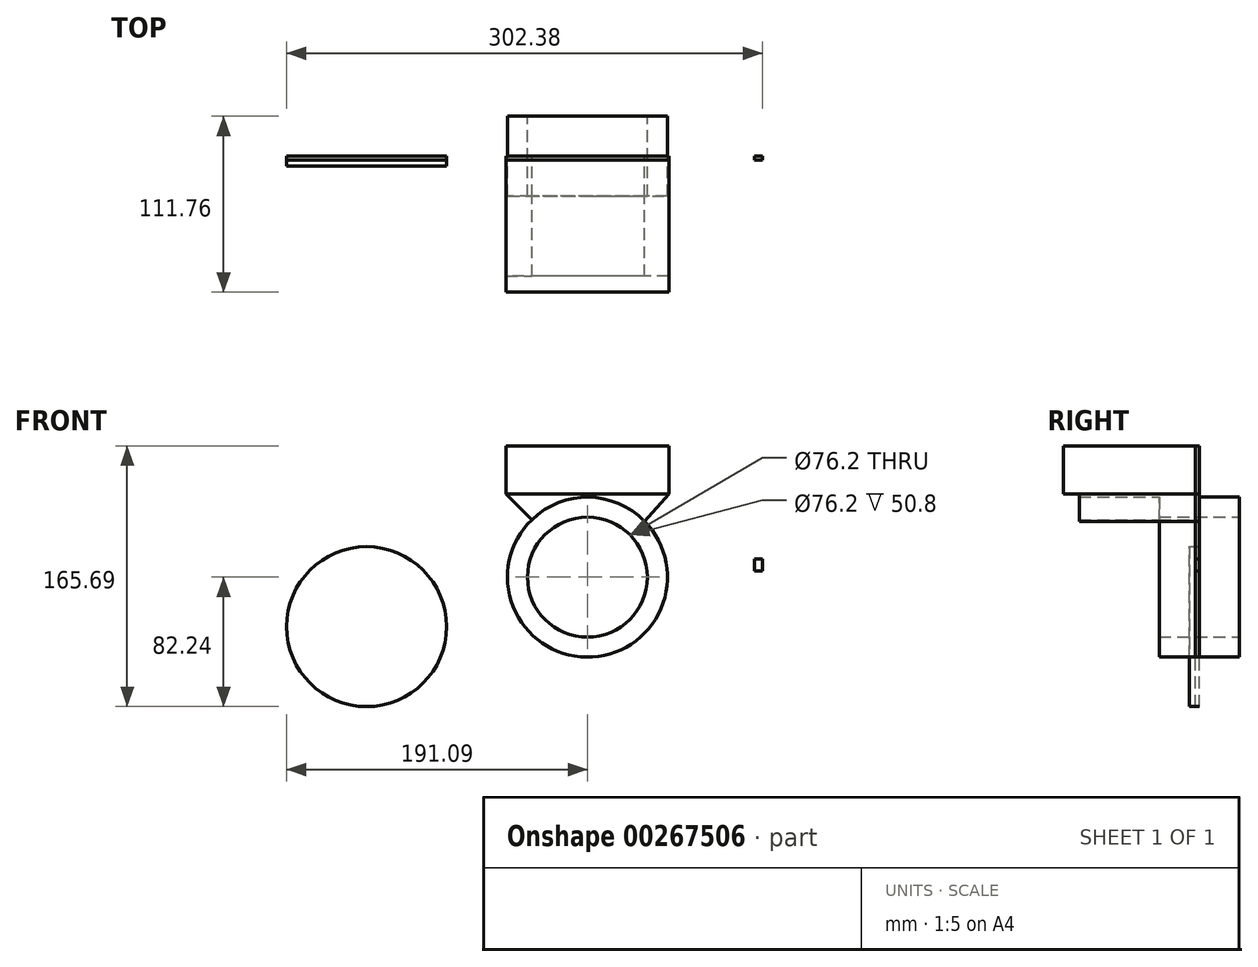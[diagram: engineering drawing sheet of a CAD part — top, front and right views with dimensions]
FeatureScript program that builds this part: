
annotation { "Feature Type Name" : "Feature", "Feature Type Description" : "" }
export const myFeature = defineFeature(function(context is Context, id is Id, definition is map)
    precondition{}
    {
        {
            var Q0;
            Q0=qCreatedBy(makeId("Front.planeOp"),FACE);
            var sketch = newSketch(context, id + "F0", { "sketchPlane" : qUnion([Q0])});
            skCircle(sketch, "E0", {"center": v(0, 0) * mm, "radius": 50.8 * mm});
            skCircle(sketch, "E1", {"center": v(0, 0) * mm, "radius": 38.1 * mm});
            skLineSegment(sketch, "E2.bottom", {"start": v(51.8, 83.45) * mm, "end": v(-51.8, 83.45) * mm});
            skLineSegment(sketch, "E2.top", {"start": v(51.8, 52.8) * mm, "end": v(-51.8, 52.8) * mm});
            skLineSegment(sketch, "E2.left", {"start": v(51.8, 83.45) * mm, "end": v(51.8, 52.8) * mm});
            skLineSegment(sketch, "E2.right", {"start": v(-51.8, 83.45) * mm, "end": v(-51.8, 52.8) * mm});
            skPoint(sketch, "E2.middle", {"position": v(0, 68.12) * mm});
            skLineSegment(sketch, "E3", {"start": v(-51.8, 52.8) * mm, "end": v(-35.37, 36.47) * mm});
            skLineSegment(sketch, "E4", {"start": v(51.8, 52.8) * mm, "end": v(36.34, 35.5) * mm});
            skCircle(sketch, "E5", {"center": v(-140.29, -31.44) * mm, "radius": 50.8 * mm});
            skLineSegment(sketch, "E6.bottom", {"start": v(106.2, 11.62) * mm, "end": v(111.29, 11.62) * mm});
            skLineSegment(sketch, "E6.top", {"start": v(106.2, 4) * mm, "end": v(111.29, 4) * mm});
            skLineSegment(sketch, "E6.left", {"start": v(106.2, 11.62) * mm, "end": v(106.2, 4) * mm});
            skLineSegment(sketch, "E6.right", {"start": v(111.29, 11.62) * mm, "end": v(111.29, 4) * mm});
            skPoint(sketch, "E6.middle", {"position": v(108.75, 7.81) * mm});
            skSolve(sketch);
        }
        {
            var Q0;
            Q0=makeQuery(id+"F0.imprint","IMPRINT",FACE,{"disambiguationData":[TD([[makeQuery(id+"F0.imprint","IMPRINT",EDGE,{"derivedFrom":sQuery(id+"F0.wireOp",EDGE,"E1")}),-1.0]])]});
            extrude(context, id + "F1", {"entities" : qUnion([Q0]), "endBound" : BoundingType.SYMMETRIC, "depth" : 50.8 * mm});
        }
        {
            var Q0;
            {var subQ0=sQuery(id+"F0.wireOp",EDGE,"E3");Q0=makeQuery(id+"F0.imprint","IMPRINT",FACE,{"disambiguationData":[TD([[makeQuery(id+"F0.imprint","IMPRINT",EDGE,{"derivedFrom":subQ0}),1.0]])]});}
            var Q1;
            {var subQ0=sQuery(id+"F0.wireOp",EDGE,"E4");Q1=makeQuery(id+"F0.imprint","IMPRINT",FACE,{"disambiguationData":[TD([[makeQuery(id+"F0.imprint","IMPRINT",EDGE,{"derivedFrom":subQ0}),-1.0]])]});}
            extrude(context, id + "F2", {"entities" : qUnion([Q0, Q1]), "operationType" : NewBodyOperationType.ADD, "depth" : 76.2 * mm});
        }
        {
            var Q0;
            Q0=makeQuery(id+"F0.imprint","IMPRINT",FACE,{"disambiguationData":[TD([[makeQuery(id+"F0.imprint","IMPRINT",EDGE,{"derivedFrom":sQuery(id+"F0.wireOp",EDGE,"E2.bottom")}),1.0]])]});
            extrude(context, id + "F3", {"entities" : qUnion([Q0]), "operationType" : NewBodyOperationType.ADD, "depth" : 86.36 * mm});
        }
        {
            var Q0;
            Q0=makeQuery(id+"F0.imprint","IMPRINT",FACE,{"disambiguationData":[TD([[makeQuery(id+"F0.imprint","IMPRINT",EDGE,{"derivedFrom":sQuery(id+"F0.wireOp",EDGE,"E5")}),1.0]])]});
            extrude(context, id + "F4", {"entities" : qUnion([Q0]), "depth" : 6.35 * mm});
        }
        {
            var Q0;
            Q0 = qSketchRegion(id + "F0", true);
            extrude(context, id + "F5", {"entities" : qUnion([Q0]), "depth" : 2.54 * mm});
        }
    });
